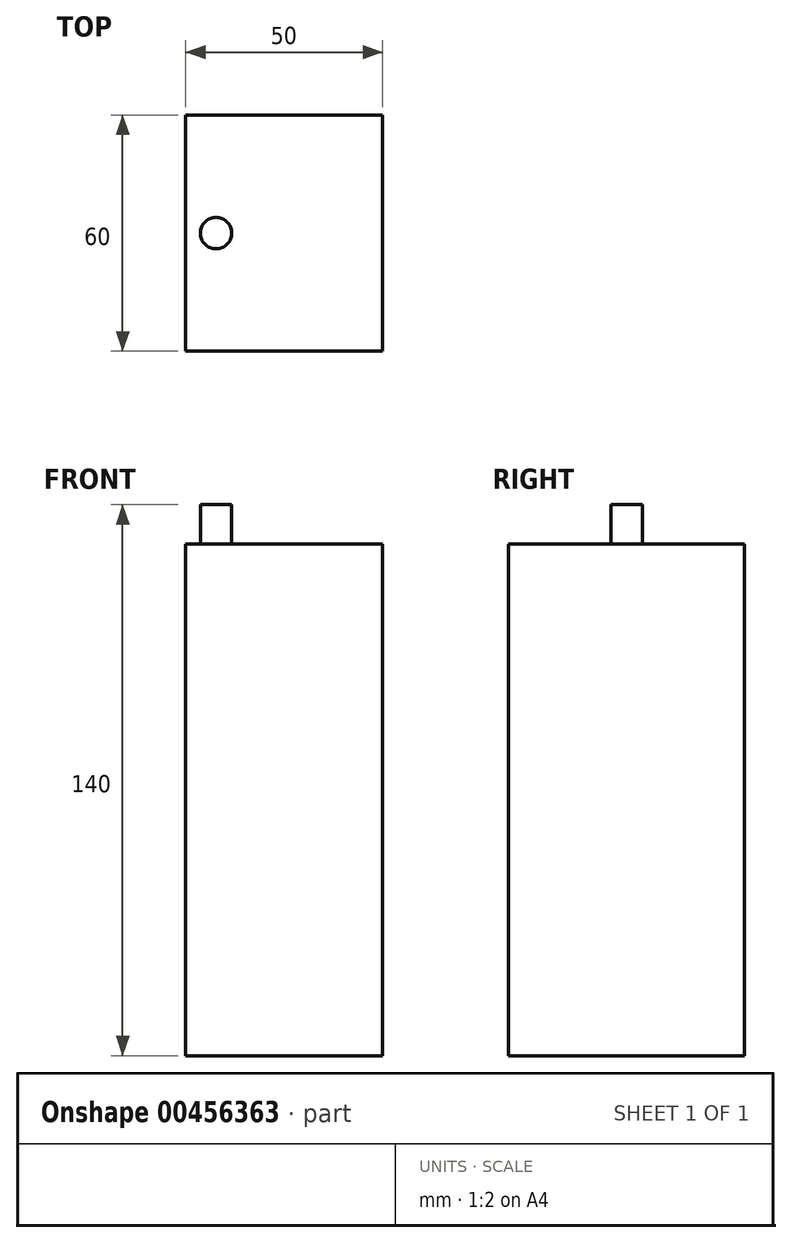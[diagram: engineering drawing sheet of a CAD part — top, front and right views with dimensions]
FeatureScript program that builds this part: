
annotation { "Feature Type Name" : "Feature", "Feature Type Description" : "" }
export const myFeature = defineFeature(function(context is Context, id is Id, definition is map)
    precondition{}
    {
        {
            var Q0;
            Q0=qCreatedBy(makeId("Front.planeOp"),FACE);
            var sketch = newSketch(context, id + "F0", { "sketchPlane" : qUnion([Q0])});
            skLineSegment(sketch, "E0.bottom", {"start": v(-25.62, 0) * mm, "end": v(24.38, 0) * mm});
            skLineSegment(sketch, "E0.top", {"start": v(-25.62, 130) * mm, "end": v(24.38, 130) * mm});
            skLineSegment(sketch, "E0.left", {"start": v(-25.62, 0) * mm, "end": v(-25.62, 130) * mm});
            skLineSegment(sketch, "E0.right", {"start": v(24.38, 0) * mm, "end": v(24.38, 130) * mm});
            skSolve(sketch);
        }
        {
            var Q0;
            Q0 = qSketchRegion(id + "F0", true);
            extrude(context, id + "F1", {"entities" : qUnion([Q0]), "depth" : 30 * mm, "hasSecondDirection" : true, "secondDirectionOppositeDirection" : true, "secondDirectionDepth" : 30 * mm, "offsetDistance" : 25 * mm});
        }
        {
            var Q0;
            Q0=makeQuery(id+"F1.opExtrude","SWEPT_FACE",FACE,{"disambiguationData":[OSD([sQuery(id+"F0.wireOp",EDGE,"E0.top")])]});
            var sketch = newSketch(context, id + "F2", { "sketchPlane" : qUnion([Q0])});
            skCircle(sketch, "E1", {"center": v(-17.92, 0) * mm, "radius": 4 * mm});
            skPoint(sketch, "E1.centerSnap0", {"position": v(-25.62, 0) * mm});
            skSolve(sketch);
        }
        {
            var Q0;
            Q0=makeQuery(id+"F2.imprint","IMPRINT",FACE,{"disambiguationData":[TD([[makeQuery(id+"F2.imprint","IMPRINT",EDGE,{"derivedFrom":sQuery(id+"F2.wireOp",EDGE,"E1")}),1.0]])]});
            extrude(context, id + "F3", {"entities" : qUnion([Q0]), "operationType" : NewBodyOperationType.ADD, "depth" : 10 * mm});
        }
    });
